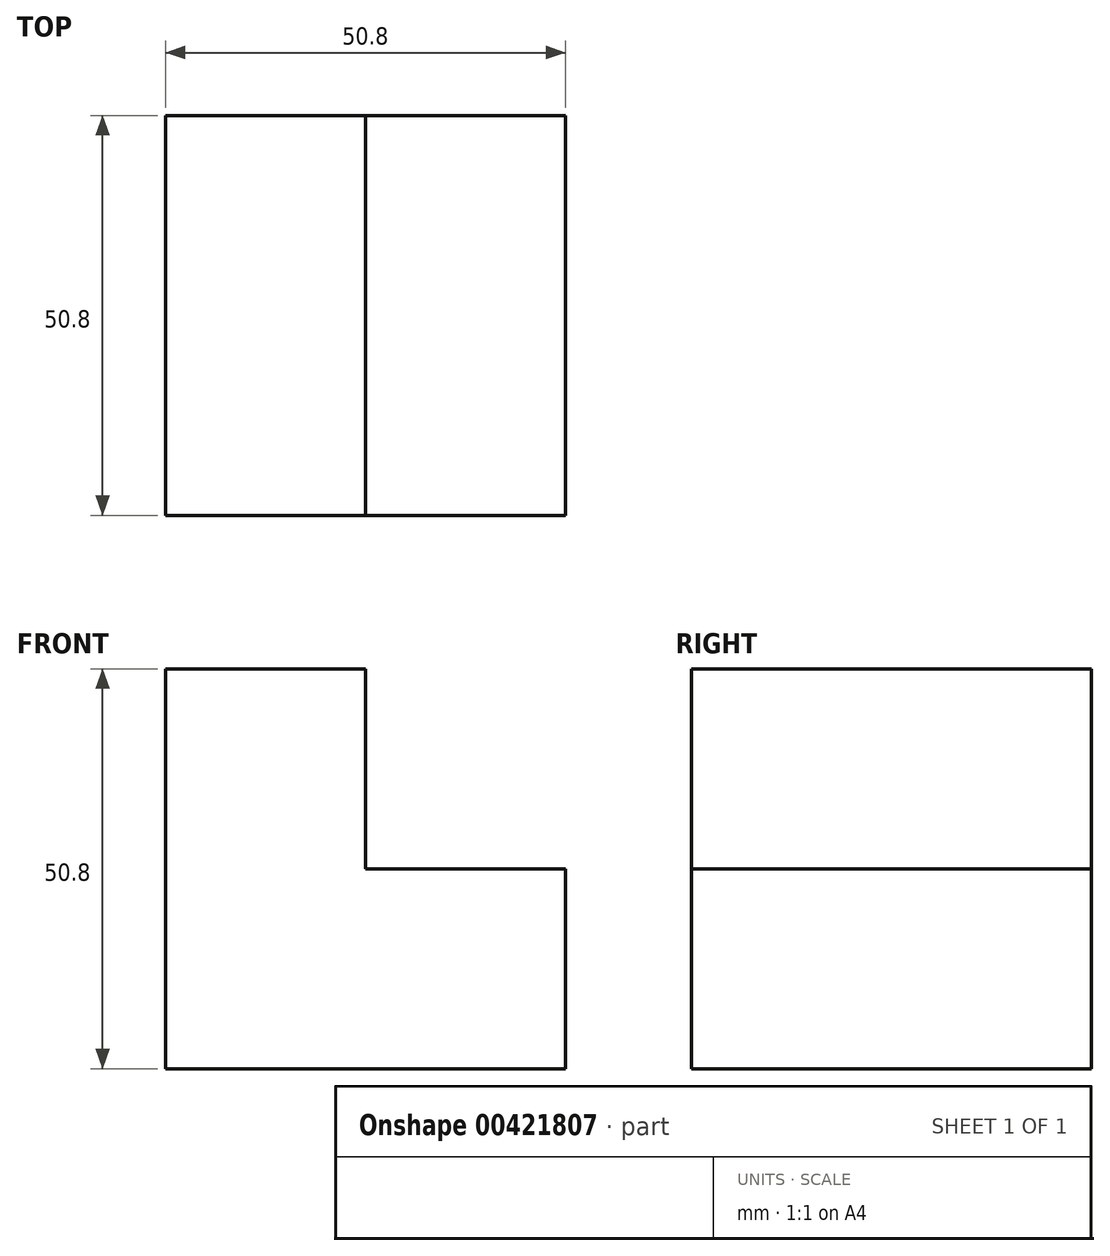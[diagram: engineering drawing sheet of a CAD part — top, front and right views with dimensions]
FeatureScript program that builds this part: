
annotation { "Feature Type Name" : "Feature", "Feature Type Description" : "" }
export const myFeature = defineFeature(function(context is Context, id is Id, definition is map)
    precondition{}
    {
        {
            var Q0;
            Q0=qCreatedBy(makeId("Front.planeOp"),FACE);
            var sketch = newSketch(context, id + "F0", { "sketchPlane" : qUnion([Q0])});
            skLineSegment(sketch, "E0", {"start": v(0, 0) * mm, "end": v(-50.8, 0) * mm});
            skLineSegment(sketch, "E1", {"start": v(-50.8, 0) * mm, "end": v(-50.8, 50.8) * mm});
            skLineSegment(sketch, "E2", {"start": v(-50.8, 50.8) * mm, "end": v(-25.4, 50.8) * mm});
            skLineSegment(sketch, "E3", {"start": v(-25.4, 50.8) * mm, "end": v(-25.4, 25.4) * mm});
            skPoint(sketch, "E3.endSnap0", {"position": v(-25.4, 0) * mm});
            skLineSegment(sketch, "E4", {"start": v(-25.4, 25.4) * mm, "end": v(0, 25.4) * mm});
            skLineSegment(sketch, "E5", {"start": v(0, 25.4) * mm, "end": v(0, 0) * mm});
            skSolve(sketch);
        }
        {
            var Q0;
            Q0 = qSketchRegion(id + "F0", true);
            extrude(context, id + "F1", {"entities" : qUnion([Q0]), "depth" : 50.8 * mm});
        }
    });
